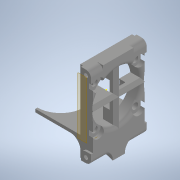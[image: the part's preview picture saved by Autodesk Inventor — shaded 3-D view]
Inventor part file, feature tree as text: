
AUTODESK INVENTOR PART (.ipt)
format: ipt  version: 2022 (Build 260153000, 153)  size: 455,680 bytes
history: native  units: mm
features: reference x16, other x13, sketch x11, extrude x10, fillet x3, plane x2, chamfer x2, mirror x1
ambient origin geometry x8: Origin, YZ Plane, XZ Plane, XY Plane, X Axis, Y Axis, Z Axis, Center Point
bodies: Solid1 (feature_tree)
feature tree (58):
  extrude  "Extrusion1"  Depth=25.5mm
  plane  "Work Plane1"
  extrude  "Extrusion2"  Depth=3.0mm
  extrude  "Extrusion3"  Depth=3.0mm
  sketch  "Sketch4"  dims[d6=2.75mm d7=3.0mm]
  extrude  "Extrusion4"  Depth=3.0mm
  mirror  "Mirror2"
  extrude  "Extrusion5"  Depth=3.0mm TaperAngle=0.0deg
  extrude  "Extrusion6"  Depth=3.0mm
  extrude  "Extrusion7"  Depth=14.5mm TaperAngle=0.0deg
  extrude  "Extrusion8"  Depth=14.5mm TaperAngle=0.0deg
  chamfer  "Chamfer1"  Distance=3.0mm
  fillet  "Fillet1"  Radius=30.0mm
  fillet  "Fillet2"  Radius=6.0mm
  chamfer  "Chamfer2"  Distance=6.0mm
  plane  "Work Plane2"
  extrude  "Extrusion9"  Depth=3.175mm TaperAngle=0.0deg
  fillet  "Fillet3"  Radius=6.0mm
  extrude  "Extrusion10"  Depth=3.175mm TaperAngle=0.0deg
  sketch  "Sketch1"  dims[d0=25.5mm d1=25.5mm]
  sketch  "Sketch2"  dims[d2=24.0mm d3=3.0mm]
  reference  "Reference1"
  sketch  "Sketch3"  dims[d4=3.0mm d5=20.0mm]
  reference  "Reference2"
  reference  "Reference3"
  sketch  "Sketch5"  dims[d8=3.0mm d9=6.25mm d10=0.0mm]
  reference  "Reference4"
  reference  "Reference5"
  reference  "Reference6"
  sketch  "Sketch6"  dims[d11=3.0mm d12=3.0mm]
  sketch  "Sketch7"  dims[d13=1.0mm d14=14.5mm d15=0.0mm]
  reference  "Reference8"
  sketch  "Sketch8"  dims[d16=4.5mm d17=0.0mm d18=14.5mm d19=0.0mm]
  reference  "Reference9"
  reference  "Reference10"
  reference  "Reference11"
  reference  "Reference12"
  reference  "Reference14"
  reference  "Reference15"
  sketch  "Sketch9"  dims[d20=135.0deg d21=3.0mm d22=0.0mm d23=30.0mm d24=0.0mm d25=6.0mm]
  sketch  "Sketch10"  dims[d26=6.0mm]
  reference  "Reference16"
  reference  "Reference17"
  reference  "Reference18"
  sketch  "Sketch11"  dims[d27=6.0mm d28=6.0mm d29=2.0mm d30=0.0mm d31=6.0mm d32=6.0mm d33=0.0mm d34=6.0mm d35=3.0mm d36=45.0deg d37=3.0mm d38=2.0mm d39=1.45mm d40=2.0mm d41=45.0deg d42=11.5mm d43=0.25mm d44=1.5mm d45=0.0mm d46=5.0mm d47=13.0mm d48=3.175mm d49=0.0mm]
  other  "Volcano_Printhead.iam"
  other  "4010 turbo fan v3:3"
  other  "sherpa_mini_release1:1"
  other  "Assembly246"
  other  "4010 turbo fan v3:2"
  other  "hex_socket_button_head_M3x10:3"
  other  "hex_socket_button_head_M3x10:4"
  other  "hex_socket_button_head_M3x10:1"
  other  "hex_socket_button_head_M3x10:2"
  other  "volcano tool.iam"
  other  "v6_Clamp V2:1"
  other  "E3D-VOLCANO-1.75-MO:1"
  other  "4010 turbo fan v3:1"
